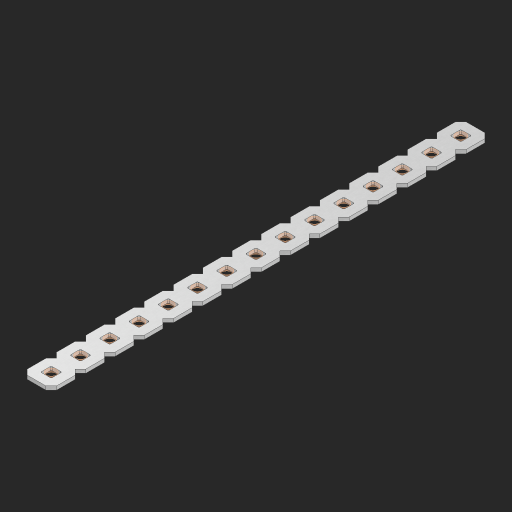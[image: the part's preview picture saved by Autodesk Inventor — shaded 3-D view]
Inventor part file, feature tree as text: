
AUTODESK INVENTOR PART (.ipt)
format: ipt  version: 2023 (Build 270158000, 158)  size: 429,568 bytes
history: native  units: in
note: dims shown in document units (in); Inventor stores cm internally (conversion verified against a paired STEP export)
features: other x16, extrude x14, sketch x2, pattern_linear x1
ambient origin geometry x8: Origin, YZ Plane, XZ Plane, XY Plane, X Axis, Y Axis, Z Axis, Center Point
bodies: Solid1 (feature_tree), Body (feature_tree)
feature tree (33):
  pattern_linear  "Rectangular Pattern1"  Spacing1=0.09in  [1 undecoded]
  sketch  "Sketch1"  dims[d1=0.5in]
  sketch  "Sketch2"  dims[d2=0.182in d3=0.09in d4=0.09in d5=0.09in d6=0.09in d7=0.09in d8=0.09in d9=0.09in d10=0.09in d11=0.02in d13=0.0in d14=0.172in d15=0.0625in d16=0.0in d19=0.5in d22=0.5in]
  other  "Srf1"
  other  "Srf126"
  other  "Srf127"
  other  "Srf128"
  other  "Srf129"
  other  "Srf130"
  other  "Srf131"
  other  "Srf250"
  other  "Srf251"
  other  "Srf252"
  other  "Srf253"
  other  "Srf254"
  other  "Srf255"
  other  "Srf256"
  other  "Srf257"
  other  "Circle"
  extrude  "ExtrusionSrf126"  Depth=0.09in
  extrude  "ExtrusionSrf127"  Depth=0.09in
  extrude  "ExtrusionSrf128"  Depth=0.09in
  extrude  "ExtrusionSrf129"  Depth=0.09in
  extrude  "ExtrusionSrf130"  Depth=0.09in
  extrude  "ExtrusionSrf131"  Depth=0.09in
  extrude  "ExtrusionSrf250"  Depth=0.09in
  extrude  "ExtrusionSrf251"  Depth=0.02in
  extrude  "ExtrusionSrf252"  TaperAngle=0.0deg  [1 undecoded]
  extrude  "ExtrusionSrf253"  Depth=0.5in
  extrude  "ExtrusionSrf254"  Depth=0.0625in TaperAngle=0.0deg
  extrude  "ExtrusionSrf255"  Depth=0.5in
  extrude  "ExtrusionSrf256"  Depth=0.5in
  extrude  "ExtrusionSrf257"  [1 undecoded]
note: 3 required parameter values undecoded (feature->parameter linkage not recoverable at this tier; creation-order binding heuristic only, values carry confidence <= 0.55)
